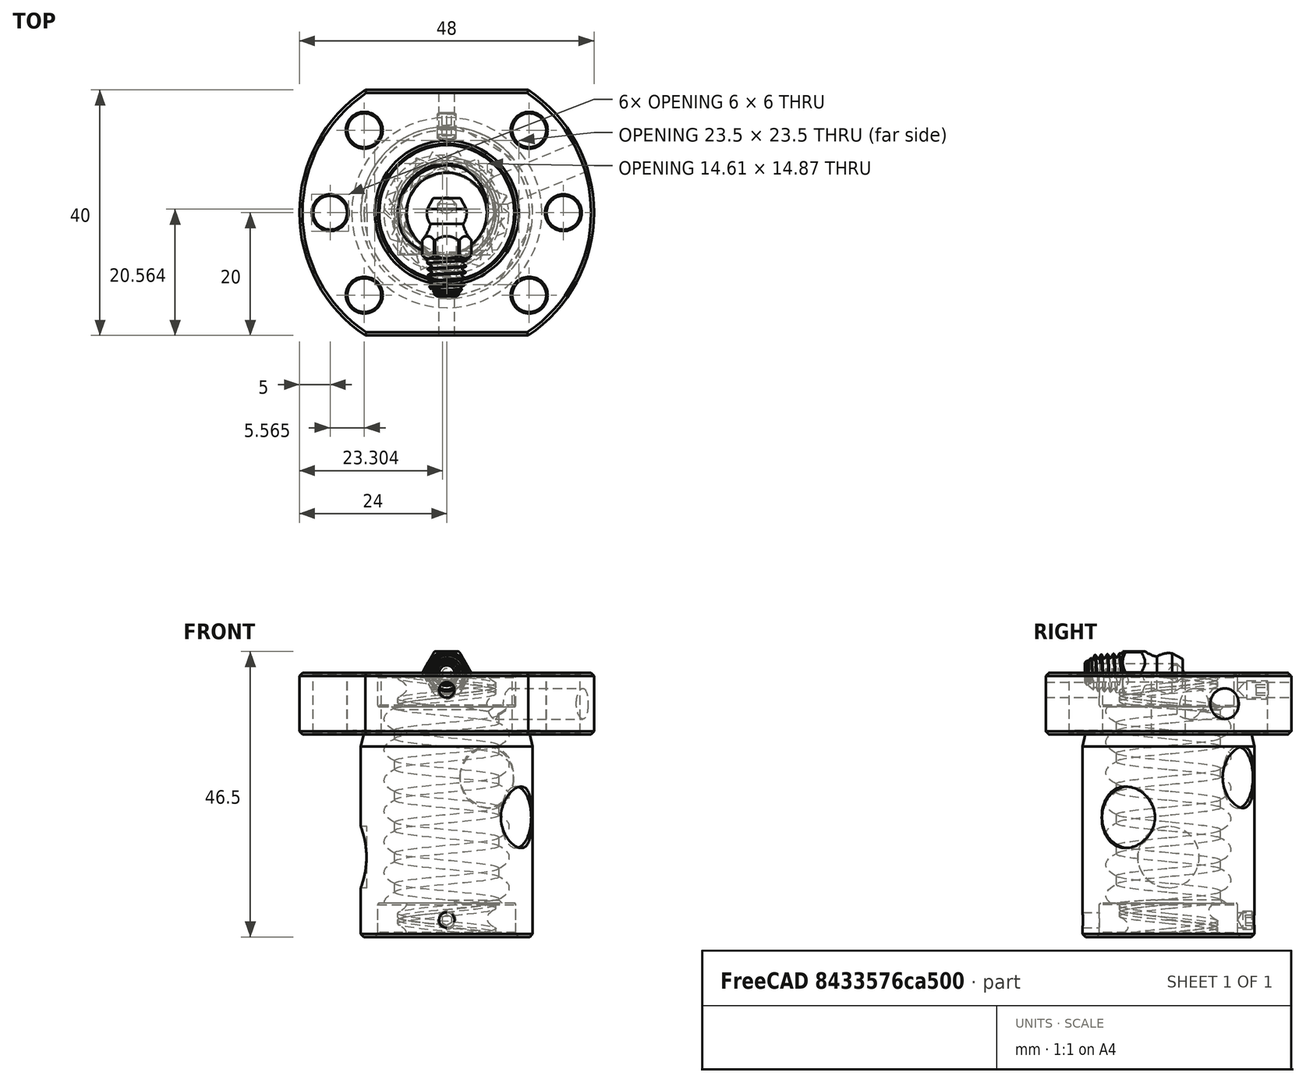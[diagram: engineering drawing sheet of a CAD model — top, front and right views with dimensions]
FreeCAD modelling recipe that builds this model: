
FCSTD DOCUMENT  (FreeCAD 0.21R38887 (Git))
Label: SFU1605
License: All rights reserved
LicenseURL: http://en.wikipedia.org/wiki/All_rights_reserved
objects: Part::Feature×7, Part::FeaturePython×6, App::Link×2, App::Part×2, App::FeaturePython×2
note: 12 computed .brp shape members not serialized (recipe doc carries the construction recipe); baked Part::Feature solids carry a one-line shape summary decoded from their .brp

FEATURE [Part::Feature] Solid  label="SFU1605-3"
  InvalidShape = false
  TreeRank = 8
  ValidateShape = false
  shape: bbox 48 x 40 x 43 mm, 126 faces (baked)
FEATURE [Part::Feature] Solid001  label="SFU1605 Washer Front"
  InvalidShape = false
  TreeRank = 9
  ValidateShape = false
  shape: bbox 22.5 x 22.5 x 11.47 mm, 23 faces (baked)
FEATURE [Part::Feature] Solid002  label="SFU1605 Washer Back"
  InvalidShape = false
  TreeRank = 10
  ValidateShape = false
  shape: bbox 22.5 x 22.5 x 11.47 mm, 22 faces (baked)
FEATURE [Part::Feature] Solid003  label="socket set screw cone point_iso_ISO 4027 - M3 x 5-N"
  InvalidShape = false
  Placement = pos=(0,16.25,-2.75) rot=(0,0,-1;1.5708rad)
  TreeRank = 11
  ValidateShape = false
  shape: bbox 3 x 5 x 3 mm, 14 faces (baked)
FEATURE [Part::Feature] Solid004  label="socket set screw cone point_iso_ISO 4027 - M3 x 2.5-N"
  InvalidShape = false
  Placement = pos=(0,13.75,-40.25) rot=(0,0,-1;1.5708rad)
  TreeRank = 12
  ValidateShape = false
  shape: bbox 3 x 2.5 x 3 mm, 14 faces (baked)
FEATURE [App::Link] Link  label="socket set screw cone point_iso_ISO 4027 - M3 x 5-N001"
  AutoLinkLabel = true
  AutoPlacement = true
  LinkPlacement = pos=(4e-16,-16.25,-2.75) rot=(0.707107,0.707107,0;3.14159rad)
  LinkedObject = -> Solid003
  Placement = pos=(4e-16,-16.25,-2.75) rot=(0.707107,0.707107,0;3.14159rad)
  SyncGroupVisibility = false
  TreeRank = 13
  _LinkVersion = 1
FEATURE [App::Link] Link001  label="socket set screw cone point_iso_ISO 4027 - M3 x 2.5-N001"
  AutoLinkLabel = true
  AutoPlacement = true
  LinkPlacement = pos=(0,-13.75,-40.25) rot=(0,0,1;1.5708rad)
  LinkedObject = -> Solid004
  Placement = pos=(0,-13.75,-40.25) rot=(0,0,1;1.5708rad)
  SyncGroupVisibility = false
  TreeRank = 14
  _LinkVersion = 1
FEATURE [Part::Feature] Solid005  label="Grease Nipple A_A M6x1.00"
  InvalidShape = false
  TreeRank = 21
  ValidateShape = false
  shape: bbox 9.143 x 16.91 x 9.143 mm, 68 faces (baked)
FEATURE [Part::Feature] Solid006  label="Steel Ball_O 2.50"
  InvalidShape = false
  Placement = pos=(0,1.19521,0) rot=(0,0,1;0rad)
  TreeRank = 22
  ValidateShape = false
  shape: bbox 2.5 x 2.5 x 2.5 mm, 2 faces (baked)
FEATURE [App::Part] Part  label="Grease Nipple A M6x1.00"
  ClaimAllChildren = false
  ExportMode = 1
  Group = -> [Solid005,Solid006]
  Origin = -> Origin
  Placement = pos=(29.0604,12.0372,-5) rot=(0.485653,0.726831,-0.485653;1.88458rad)
  TreeRank = 24
  _ExportChildren = -> [Solid005,Solid006]
  _GroupVersion = 1
FEATURE [App::Part] Part001  label="SFU1605-004"
  ClaimAllChildren = false
  ExportMode = 1
  Group = -> [Solid,Solid001,Solid002,Solid003,Solid004,Link,Link001,Part]
  Origin = -> Origin001
  TreeRank = 26
  _ExportChildren = -> [Solid,Solid001,Solid002,Solid003,Solid004,Link,Link001,Part]
  _GroupVersion = 1
FEATURE [App::FeaturePython] Constraints  # WARN: FeaturePython — macro-defined, semantics opaque (R4)
  TreeRank = 28
  _LinkVersion = 1
  _Version = 1
FEATURE [Part::FeaturePython] Parts  label="Деталі"  # WARN: FeaturePython — macro-defined, semantics opaque (R4)
  Group = -> [Part001]
  GroupMode = 0
  InvalidShape = false
  TreeRank = 30
  ValidateShape = false
  _LinkVersion = 1
FEATURE [Part::FeaturePython] Assembly  label="SFU1606"  # WARN: FeaturePython — macro-defined, semantics opaque (R4)
  AutoRelax = true
  BuildShape = 0
  Freeze = false
  Group = -> [Constraints,Elements,Parts]
  InvalidShape = false
  TreeRank = 27
  ValidateShape = false
  Verbose = false
  _LinkVersion = 1
  _SolverType = 1
  _Version = 1
FEATURE [App::FeaturePython] Elements  # WARN: FeaturePython — macro-defined, semantics opaque (R4)
  Group = -> [Element,Element001,Element002,Element003]
  TreeRank = 29
  _LinkVersion = 1
FEATURE [Part::FeaturePython] Element  # link proxy (typed FeaturePython)
  Detach = false
  InvalidShape = false
  LinkTransform = true
  LinkedObject = -> Part001 [Solid.Face63]
  TreeRank = 31
  ValidateShape = false
  _LinkVersion = 1
  _Parent = -> Elements
FEATURE [Part::FeaturePython] Element001  # link proxy (typed FeaturePython)
  Detach = false
  InvalidShape = false
  LinkTransform = true
  LinkedObject = -> Part001 [Solid.Face72]
  TreeRank = 32
  ValidateShape = false
  _LinkVersion = 1
  _Parent = -> Elements
FEATURE [Part::FeaturePython] Element002  # link proxy (typed FeaturePython)
  Detach = false
  InvalidShape = false
  LinkTransform = true
  LinkedObject = -> Part001 [Solid.Edge227]
  TreeRank = 33
  ValidateShape = false
  _LinkVersion = 1
  _Parent = -> Elements
FEATURE [Part::FeaturePython] Element003  # link proxy (typed FeaturePython)
  Detach = false
  InvalidShape = false
  LinkTransform = true
  LinkedObject = -> Part001 [Solid.Edge127]
  TreeRank = 34
  ValidateShape = false
  _LinkVersion = 1
  _Parent = -> Elements
